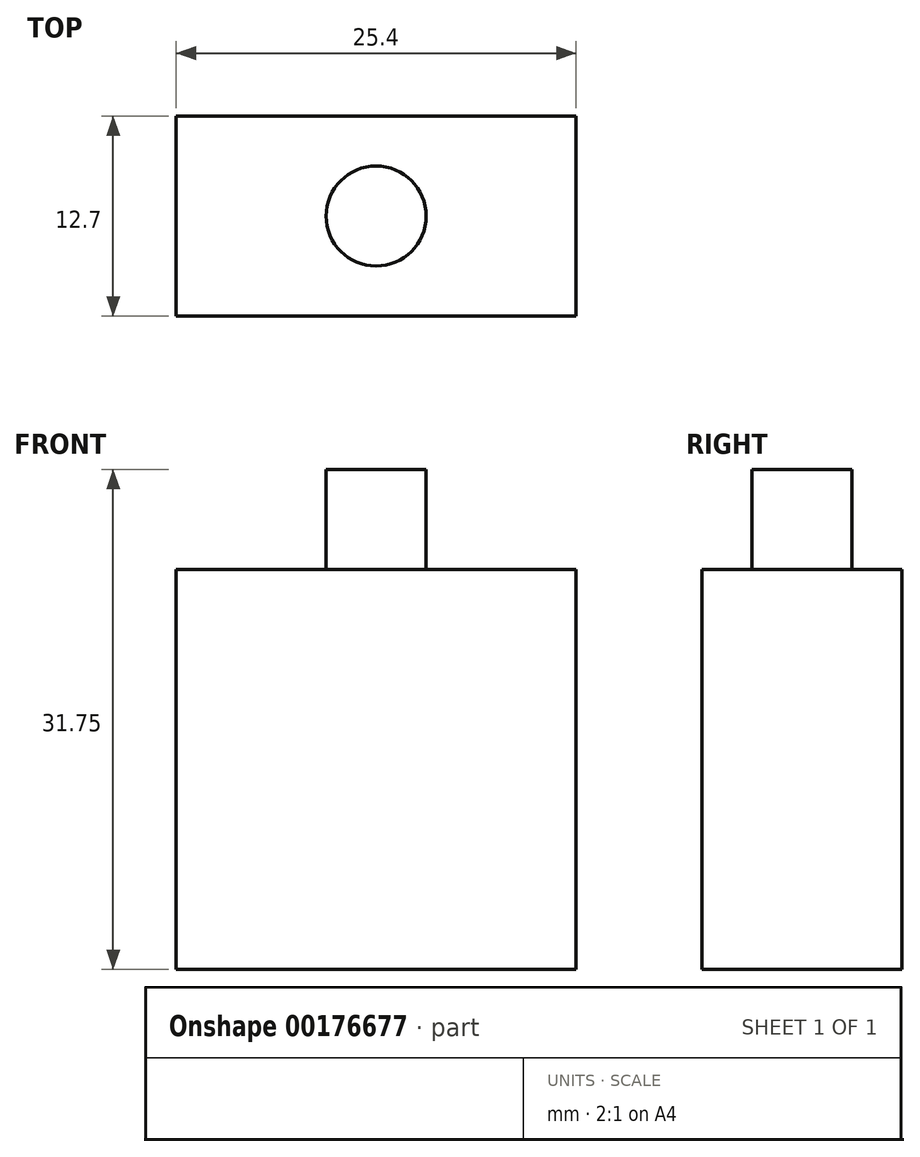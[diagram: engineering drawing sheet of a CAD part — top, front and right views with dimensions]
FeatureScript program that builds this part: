
annotation { "Feature Type Name" : "Feature", "Feature Type Description" : "" }
export const myFeature = defineFeature(function(context is Context, id is Id, definition is map)
    precondition{}
    {
        {
            var Q0;
            Q0=qCreatedBy(makeId("Front.planeOp"),FACE);
            var sketch = newSketch(context, id + "F0", { "sketchPlane" : qUnion([Q0])});
            skLineSegment(sketch, "E0.bottom", {"start": v(-25.4, 25.4) * mm, "end": v(0, 25.4) * mm});
            skLineSegment(sketch, "E0.top", {"start": v(-25.4, 0) * mm, "end": v(0, 0) * mm});
            skLineSegment(sketch, "E0.left", {"start": v(-25.4, 25.4) * mm, "end": v(-25.4, 0) * mm});
            skLineSegment(sketch, "E0.right", {"start": v(0, 25.4) * mm, "end": v(0, 0) * mm});
            skSolve(sketch);
        }
        {
            var Q0;
            Q0 = qSketchRegion(id + "F0", true);
            extrude(context, id + "F1", {"entities" : qUnion([Q0]), "depth" : 12.7 * mm});
        }
        {
            var Q0;
            Q0=makeQuery(id+"F1.opExtrude","SWEPT_FACE",FACE,{"disambiguationData":[OSD([sQuery(id+"F0.wireOp",EDGE,"E0.bottom")])]});
            var sketch = newSketch(context, id + "F2", { "sketchPlane" : qUnion([Q0])});
            skCircle(sketch, "E1", {"center": v(-12.7, -6.35) * mm, "radius": 3.18 * mm});
            skPoint(sketch, "E1.centerSnap0", {"position": v(-25.4, -6.35) * mm});
            skLineSegment(sketch, "E2", {"start": v(0, -12.7) * mm, "end": v(-25.4, 0) * mm, "construction": true});
            skSolve(sketch);
        }
        {
            var Q0;
            Q0 = qSketchRegion(id + "F2", true);
            extrude(context, id + "F3", {"entities" : qUnion([Q0]), "operationType" : NewBodyOperationType.ADD, "depth" : 6.35 * mm});
        }
    });
